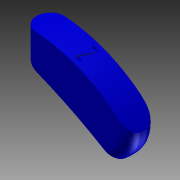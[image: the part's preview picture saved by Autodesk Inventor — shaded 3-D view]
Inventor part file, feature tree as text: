
AUTODESK INVENTOR PART (.ipt)
format: ipt  version: 2012 SP1 (Build 160190100, 190)  size: 163,328 bytes
history: native  units: in
note: dims shown in document units (in); Inventor stores cm internally (conversion verified against a paired STEP export)
features: extrude x6, sketch x6, fillet x2
ambient origin geometry x8: Origin, YZ Plane, XZ Plane, XY Plane, X Axis, Y Axis, Z Axis, Center Point
bodies: Solid1 (feature_tree)
feature tree (14):
  extrude  "Extrusion1"  Depth=0.125in
  fillet  "Fillet1"  Radius=0.104in
  fillet  "Fillet2"  Radius=0.65in
  extrude  "Extrusion2"  Depth=0.0625in TaperAngle=0.0deg
  extrude  "Extrusion3"  Depth=0.0625in TaperAngle=0.0deg
  extrude  "Extrusion4"  [1 undecoded]
  extrude  "Extrusion5"  [1 undecoded]
  extrude  "Extrusion6"  [1 undecoded]
  sketch  "Sketch1"  dims[d4=0.25in d5=0.0in d6=0.125in d7=0.104in d8=0.65in d9=0.0in]
  sketch  "Sketch2"  dims[d10=0.65in d11=0.0in d12=0.0625in d13=0.0in]
  sketch  "Sketch3"  dims[d14=0.0625in d15=0.0in d16=0.0625in d17=0.0in]
  sketch  "Sketch4"
  sketch  "Sketch5"
  sketch  "Sketch6"
note: 3 required parameter values undecoded (feature->parameter linkage not recoverable at this tier; creation-order binding heuristic only, values carry confidence <= 0.55)
